# Revit family: Plumbing-Faucet-Sloan-Valve-EBF-650
name_source: partatom
category: Plumbing Fixtures
units: mm (PartAtom-declared; Revit-internal decimal feet)

## family parameters
Cut with Voids When Loaded = No
Host = Face
OmniClass Number = 23.45.55.14
OmniClass Title = Single Faucets
Part Type = Normal
Room Calculation Point = No
Round Connector Dimension = Use Diameter
Shared = No

## types (19) — shared parameters
Assembly Code = D2010
CW Connection = Yes
CWFU = 1.5
Cold Water Connection Diameter = 0"
Default Elevation = 0"
Depth = 6 3/32"
Edition number = 1
HW Connection = Yes
HWFU = 1.5
Height = 3 5/8"
Hot Water Connection Diameter = 0"
Keynote = 15410
Manufacturer = Sloan Valve
Product data url = https://bimobject.com
URL = www.sloanvalve.com
Valve Pressure Drop = 0.00 psi
Vent Connection = No
Waste Connection = No
z_Trim Plate Length = 6 3/16"
zero-valued in all types: WFU

## per-type parameters (varying)
| type | Description | Part Number | Product Material | Water Flow | Width | z_Offset | z_Trim Plate 8 |
| EBF-650-8-BAT-BDM-CP-0.5GPM-MLM-IR-FCT | 8" Trim Plate, Battery Power Supply, Below Deck Manual Mixing Valve, Polished Chrome Finish, 0.5 gpm, Multi-Laminar Spray, Infrared Sensor, Optima® Battery-Powered Deck-Mounted Low Integrated Base Body Faucet. | 3315138BT | Sloan Valve - Finish - Polished Chrome | 1 GPM | 10 1/4" | 5/32" | Yes |
| EBF-650-8-BAT-BDT-CP-0.5GPM-MLM-IR-FCT | 8" Trim Plate, Battery Power Supply, Below Deck Thermostatic Mixing Valve, Polished Chrome Finish, 0.5 gpm, Multi-Laminar Spray, Infrared Sensor, Optima® Battery-Powered Deck-Mounted Low Integrated Base Body Faucet. | 3315184BT | Sloan Valve - Finish - Polished Chrome | 1 GPM | 10 1/4" | 5/32" | Yes |
| EBF-650-8-BAT-TEE-CP-0.5GPM-MLM-IR-FCT | 8" Trim Plate, Battery Power Supply, Back-Check Tee, Polished Chrome Finish, 0.5 gpm, Multi-Laminar Spray, Infrared Sensor, Optima® Battery-Powered Deck-Mounted Low Integrated Base Body Faucet | 3315139BT | Sloan Valve - Finish - Polished Chrome | 1 GPM | 10 1/4" | 5/32" | Yes |
| EBF-650-BAT-BDM-CP-0.35GPM-MLM-IR-FCT | Battery Power Supply, Below Deck Manual Mixing Valve, Polished Chrome Finish, 0.35 gpm, Multi-Laminar Spray, Infrared Sensor, Optima® Battery-Powered Deck-Mounted Low Integrated Base Body Faucet. | 3315326BT | Sloan Valve - Finish - Polished Chrome | 0 GPM | 6 5/16" | 0" | No |
| EBF-650-BAT-BDM-CP-0.5GPM-MLM-IR-FCT | Battery Power Supply, Below Deck Manual Mixing Valve, Polished Chrome Finish, 0.5 gpm, Multi-Laminar Spray, Infrared Sensor, Optima® Battery-Powered Deck-Mounted Low Integrated Base Body Faucet. | 3315137BT | Sloan Valve - Finish - Polished Chrome | 1 GPM | 6 5/16" | 0" | No |
| EBF-650-BAT-BDT-CP-0.35GPM-MLM-IR-FCT | Battery Power Supply, Below Deck Thermostatic Mixing Valve, Polished Chrome Finish, 0.35 gpm, Multi-Laminar Spray, Infrared Sensor, Optima® Battery-Powered Deck-Mounted Low Integrated Base Body Faucet. | 3315330BT | Sloan Valve - Finish - Polished Chrome | 1 GPM | 6 5/16" | 0" | No |
| EBF-650-BAT-BDT-CP-0.5GPM-MLM-IR-FCT | Battery Power Supply, Below Deck Thermostatic Mixing Valve, Polished Chrome Finish, 0.5 gpm, Multi-Laminar Spray, Infrared Sensor, Optima® Battery-Powered Deck-Mounted Low Integrated Base Body Faucet. | 3315183BT | Sloan Valve - Finish - Polished Chrome | 1 GPM | 6 5/16" | 0" | No |
| EBF-650-BAT-TEE-BN-0.5GPM-MLM-IR-FCT | Battery Power Supply, Back-Check Tee, Brushed Nickel Finish, 0.5 gpm, Multi-Laminar Spray, Infrared Sensor, Optima® Battery-Powered Deck-Mounted Low Integrated Base Body Faucet. | 3315249BT | Sloan Valve - Finish - Brushed Nickel | 1 GPM | 6 5/16" | 0" | No |
| EBF-650-BAT-TEE-CP-0.35GPM-MLM-IR-FCT | Battery Power Supply, Back-Check Tee, Polished Chrome Finish, 0.35 gpm, Multi-Laminar Spray, Infrared Sensor, Optima® Battery-Powered Deck-Mounted Low Integrated Base Body Faucet. | 3315322BT | Sloan Valve - Finish - Polished Chrome | 0 GPM | 6 5/16" | 0" | No |
| EBF-650-BAT-TEE-CP-0.5GPM-MLM-IR-FCT | Battery Power Supply, Back-Check Tee, Polished Chrome Finish, 0.5 gpm, Multi-Laminar Spray, Infrared Sensor, Optima® Battery-Powered Deck-Mounted Low Integrated Base Body Faucet. | 3315025BT | Sloan Valve - Finish - Polished Chrome | 1 GPM | 6 5/16" | 0" | No |
| EBF-650-BAT-TEE-GR-0.5GPM-MLM-IR-FCT | Battery Power Supply, Back-Check Tee, Graphite Finish, 0.5 gpm, Multi-Laminar Spray, Infrared Sensor, Optima® Battery-Powered Deck-Mounted Low Integrated Base Body Faucet. | 3315374BT | Sloan Valve - Finish - Graphite | 1 GPM | 6 5/16" | 0" | No |
| EBF-650-BAT-TEE-PB-0.5GPM-MLM-IR-FCT | Battery Power Supply, Back-Check Tee, Polished Brass Finish, 0.5 gpm, Multi-Laminar Spray, Infrared Sensor, Optima® Battery-Powered Deck-Mounted Low Integrated Base Body Faucet. | 3315077BT | Sloan Valve - Finish - Polished Brass | 1 GPM | 6 5/16" | 0" | No |
| EBF-650-BAT-TEE-SF-0.5GPM-MLM-IR-FCT | Battery Power Supply, Back-Check Tee, Brushed Stainless Finish, 0.5 gpm, Multi-Laminar Spray, Infrared Sensor, Optima® Battery-Powered Deck-Mounted Low Integrated Base Body Faucet. | 3315193BT | Sloan Valve - Stainless Steel - Brushed | 1 GPM | 6 5/16" | 0" | No |
| EBF-650-TUR-BDM-CP-0.35GPM-MLM-IR-FCT | Battery + Turbine Power Supply, Below Deck Manual Mixing Valve, Polished Chrome Finish, 0.35 gpm, Multi-Laminar Spray, Infrared Sensor, Optima® Battery-Powered Deck-Mounted Low Integrated Base Body Faucet. | 3315350BT | Sloan Valve - Finish - Polished Chrome | 1 GPM | 6 5/16" | 0" | No |
| EBF-650-TUR-BDM-CP-0.5GPM-MLM-IR-FCT | Battery + Turbine Power Supply, Below Deck Manual Mixing Valve, Polished Chrome Finish, 0.5 gpm, Multi-Laminar Spray, Infrared Sensor, Optima® Battery-Powered Deck-Mounted Low Integrated Base Body Faucet. | 3315348BT | Sloan Valve - Finish - Polished Chrome | 1 GPM | 6 5/16" | 0" | No |
| EBF-650-TUR-BDT-CP-0.35GPM-MLM-IR-FCT | Battery + Turbine Power Supply, Below Deck Thermostatic Mixing Valve, Polished Chrome Finish, 0.35 gpm, Multi-Laminar Spray, Infrared Sensor, Optima® Battery-Powered Deck-Mounted Low Integrated Base Body Faucet. | 3315351BT | Sloan Valve - Finish - Polished Chrome | 0 GPM | 6 5/16" | 0" | No |
| EBF-650-TUR-BDT-CP-0.5GPM-MLM-IR-FCT | Battery + Turbine Power Supply, Below Deck Thermostatic Mixing Valve, Polished Chrome Finish, 0.5 gpm, Multi-Laminar Spray, Infrared Sensor, Optima® Battery-Powered Deck-Mounted Low Integrated Base Body Faucet. | 3315349BT | Sloan Valve - Finish - Polished Chrome | 1 GPM | 6 5/16" | 0" | No |
| EBF-650-TUR-TEE-CP-0.35GPM-MLM-IR-FCT | Battery + Turbine Power Supply, Back-Check Tee, Polished Chrome Finish, 0.35 gpm, Multi-Laminar Spray, Infrared Sensor, Optima® Battery-Powered Deck-Mounted Low Integrated Base Body Faucet. | 3315347BT | Sloan Valve - Finish - Polished Chrome | 0 GPM | 6 5/16" | 0" | No |
| EBF-650-TUR-TEE-CP-0.5GPM-MLM-IR-FCT | Battery + Turbine Power Supply, Back-Check Tee, Polished Chrome Finish, 0.5 gpm, Multi-Laminar Spray, Infrared Sensor, Optima® Battery-Powered Deck-Mounted Low Integrated Base Body Faucet. | 3315346BT | Sloan Valve - Finish - Polished Chrome | 1 GPM | 6 5/16" | 0" | No |

note: column(s) folded — value = type name in every type: Model

## geometry (parser evidence)
native form markers: Sweep x7
no freeform markers — native parametric forms only
